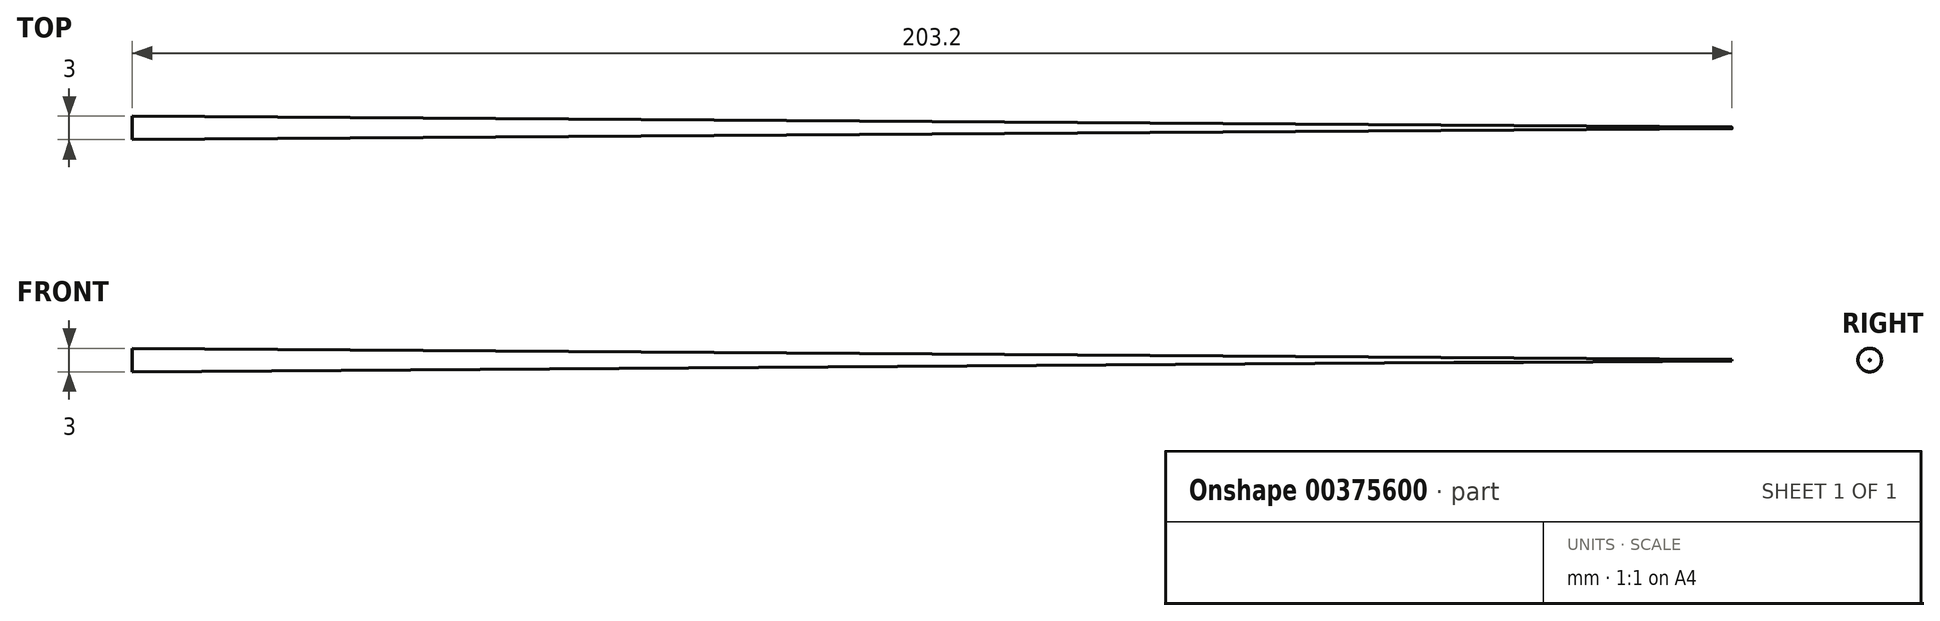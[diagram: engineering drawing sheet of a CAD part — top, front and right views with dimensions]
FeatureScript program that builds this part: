
annotation { "Feature Type Name" : "Feature", "Feature Type Description" : "" }
export const myFeature = defineFeature(function(context is Context, id is Id, definition is map)
    precondition{}
    {
        {
            var Q0;
            Q0=qCreatedBy(makeId("Right.planeOp"),FACE);
            var sketch = newSketch(context, id + "F0", { "sketchPlane" : qUnion([Q0])});
            skCircle(sketch, "E0", {"center": v(0, 0) * mm, "radius": 1.5 * mm});
            skSolve(sketch);
        }
        {
            var Q0;
            Q0=qCreatedBy(makeId("Right.planeOp"),FACE);
            cPlane(context, id + "F1", {"entities" : qUnion([Q0]), "cplaneType" : CPlaneType.OFFSET, "offset" : 203.2 * mm, "width" : 152.4 * mm, "height" : 152.4 * mm});
        }
        {
            var Q0;
            Q0=qCreatedBy(id+"F1.planeOp",FACE);
            var sketch = newSketch(context, id + "F2", { "sketchPlane" : qUnion([Q0])});
            skCircle(sketch, "E1", {"center": v(0, 0) * mm, "radius": 0.1 * mm});
            skSolve(sketch);
        }
        {
            var Q0;
            Q0=makeQuery(id+"F0.imprint","IMPRINT",FACE,{"disambiguationData":[TD([[makeQuery(id+"F0.imprint","IMPRINT",EDGE,{"derivedFrom":sQuery(id+"F0.wireOp",EDGE,"E0")}),1.0]])]});
            var Q1;
            Q1=makeQuery(id+"F2.imprint","IMPRINT",FACE,{"disambiguationData":[TD([[makeQuery(id+"F2.imprint","IMPRINT",EDGE,{"derivedFrom":sQuery(id+"F2.wireOp",EDGE,"E1")}),1.0]])]});
            loft(context, id + "F3", {"sheetProfilesArray" : [{ "sheetProfileEntities" : qUnion([Q0]) }, { "sheetProfileEntities" : qUnion([Q1]) }]});
        }
    });
